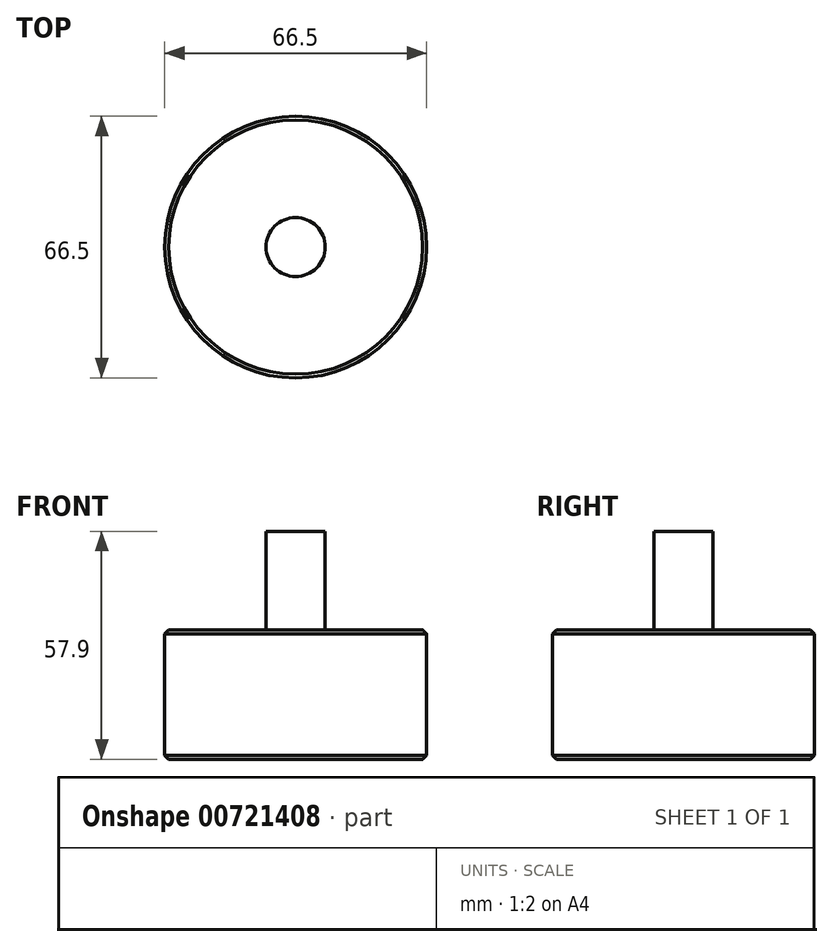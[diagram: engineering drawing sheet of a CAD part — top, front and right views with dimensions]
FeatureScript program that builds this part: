
annotation { "Feature Type Name" : "Feature", "Feature Type Description" : "" }
export const myFeature = defineFeature(function(context is Context, id is Id, definition is map)
    precondition{}
    {
        {
            var Q0;
            Q0=qCreatedBy(makeId("Top.planeOp"),FACE);
            var sketch = newSketch(context, id + "F0", { "sketchPlane" : qUnion([Q0])});
            skCircle(sketch, "E0", {"center": v(0, 0) * mm, "radius": 33.25 * mm});
            skSolve(sketch);
        }
        {
            var Q0;
            Q0=makeQuery(id+"F0.imprint","IMPRINT",FACE,{"disambiguationData":[TD([[makeQuery(id+"F0.imprint","IMPRINT",EDGE,{"derivedFrom":sQuery(id+"F0.wireOp",EDGE,"E0")}),1.0]])]});
            var sketch = newSketch(context, id + "F1", { "sketchPlane" : qUnion([Q0])});
            skSolve(sketch);
        }
        {
            var Q0;
            Q0 = qSketchRegion(id + "F0", true);
            var Q1;
            Q1=makeQuery(id+"F1.imprint","IMPRINT",FACE,{"disambiguationData":[TD([[makeQuery(id+"F1.imprint","IMPRINT",EDGE,{"derivedFrom":makeQuery(id+"F0.imprint","IMPRINT",EDGE,{"derivedFrom":sQuery(id+"F0.wireOp",EDGE,"E0")})}),1.0]])]});
            extrude(context, id + "F2", {"entities" : qUnion([Q0, Q1]), "depth" : 16.45 * mm, "offsetDistance" : 25 * mm, "hasSecondDirection" : true, "secondDirectionOppositeDirection" : true, "secondDirectionDepth" : 16.45 * mm});
        }
        {
            var Q0;
            {var subQ0=sQuery(id+"F0.wireOp",EDGE,"E0");Q0=makeQuery(id+"F2.opExtrude","CAP_EDGE",EDGE,{"disambiguationData":[OSD([subQ0]),TDD([makeQuery(id+"F0.imprint","IMPRINT",EDGE,{"derivedFrom":subQ0})])],"isStart":false});}
            var Q1;
            {var subQ0=sQuery(id+"F0.wireOp",EDGE,"E0");Q1=makeQuery(id+"F2.opExtrude","CAP_EDGE",EDGE,{"disambiguationData":[OSD([subQ0]),TDD([makeQuery(id+"F0.imprint","IMPRINT",EDGE,{"derivedFrom":subQ0})])],"isStart":true});}
            chamfer(context, id + "F3", {"entities" : qUnion([Q0, Q1]), "width" : 1 * mm, "tangentPropagation" : true});
        }
        {
            var Q0;
            {var subQ0=sQuery(id+"F0.wireOp",EDGE,"E0");Q0=makeQuery(id+"F2.opExtrude","CAP_FACE",FACE,{"disambiguationData":[OSD([subQ0]),TDD([makeQuery(id+"F0.imprint","IMPRINT",EDGE,{"derivedFrom":subQ0})])],"isStart":false});}
            var sketch = newSketch(context, id + "F4", { "sketchPlane" : qUnion([Q0])});
            skCircle(sketch, "E1", {"center": v(0, 0) * mm, "radius": 7.5 * mm});
            skSolve(sketch);
        }
        {
            var Q0;
            Q0=makeQuery(id+"F4.imprint","IMPRINT",FACE,{"disambiguationData":[TD([[makeQuery(id+"F4.imprint","IMPRINT",EDGE,{"derivedFrom":sQuery(id+"F4.wireOp",EDGE,"E1")}),1.0]])]});
            extrude(context, id + "F5", {"entities" : qUnion([Q0]), "depth" : 25 * mm, "offsetDistance" : 25 * mm});
        }
    });
